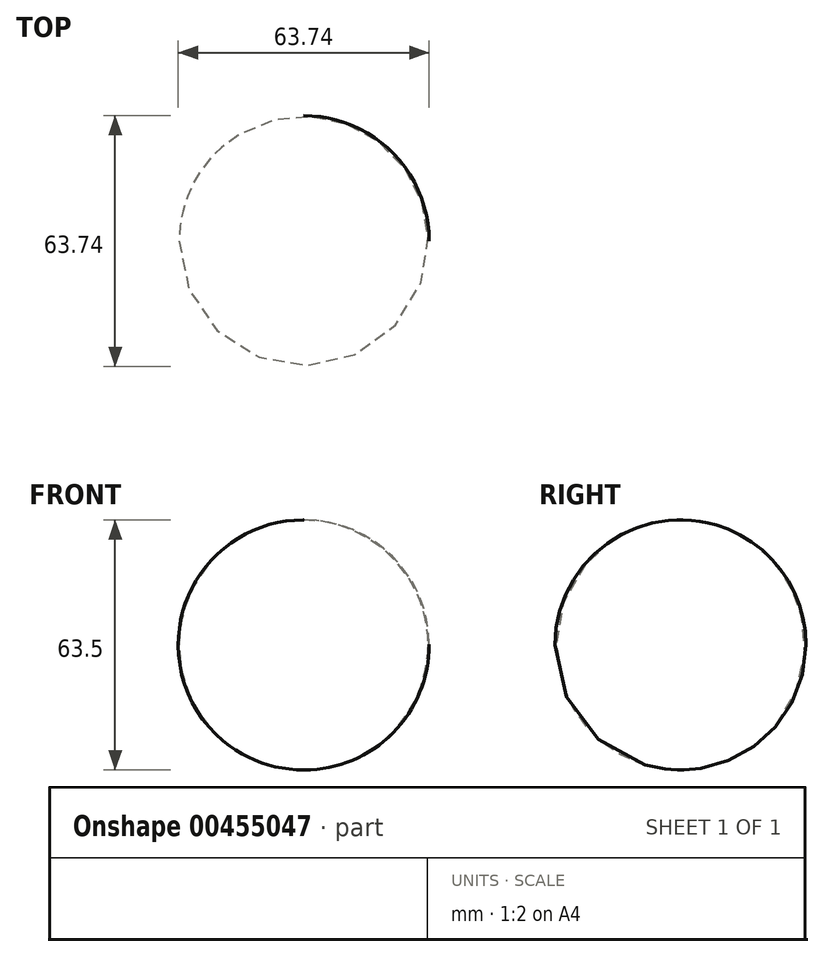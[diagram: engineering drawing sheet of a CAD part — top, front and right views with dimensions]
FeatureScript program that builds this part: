
annotation { "Feature Type Name" : "Feature", "Feature Type Description" : "" }
export const myFeature = defineFeature(function(context is Context, id is Id, definition is map)
    precondition{}
    {
        {
            var Q0;
            Q0=qCreatedBy(makeId("Front.planeOp"),FACE);
            var sketch = newSketch(context, id + "F0", { "sketchPlane" : qUnion([Q0])});
            skArc(sketch, "E0", {"start": v(-0.2, 31.75) * mm, "mid": v(-31.75, -0.09) * mm, "end": v(-0.04, -31.75) * mm});
            skLineSegment(sketch, "E1", {"start": v(-0.2, 31.75) * mm, "end": v(-0.04, -31.75) * mm});
            skSolve(sketch);
        }
        {
            var Q0;
            Q0 = qSketchRegion(id + "F0", true);
            var Q1;
            Q1=makeQuery(id+"F0.imprint","IMPRINT",FACE,{"disambiguationData":[TD([[makeQuery(id+"F0.imprint","IMPRINT",EDGE,{"derivedFrom":sQuery(id+"F0.wireOp",EDGE,"E0")}),1.0]])]});
            var Q2;
            Q2=sQuery(id+"F0.wireOp",EDGE,"E1");
            revolve(context, id + "F1", {"entities" : qUnion([Q0, Q1]), "axis" : qUnion([Q2]), "revolveType" : RevolveType.FULL});
        }
    });
